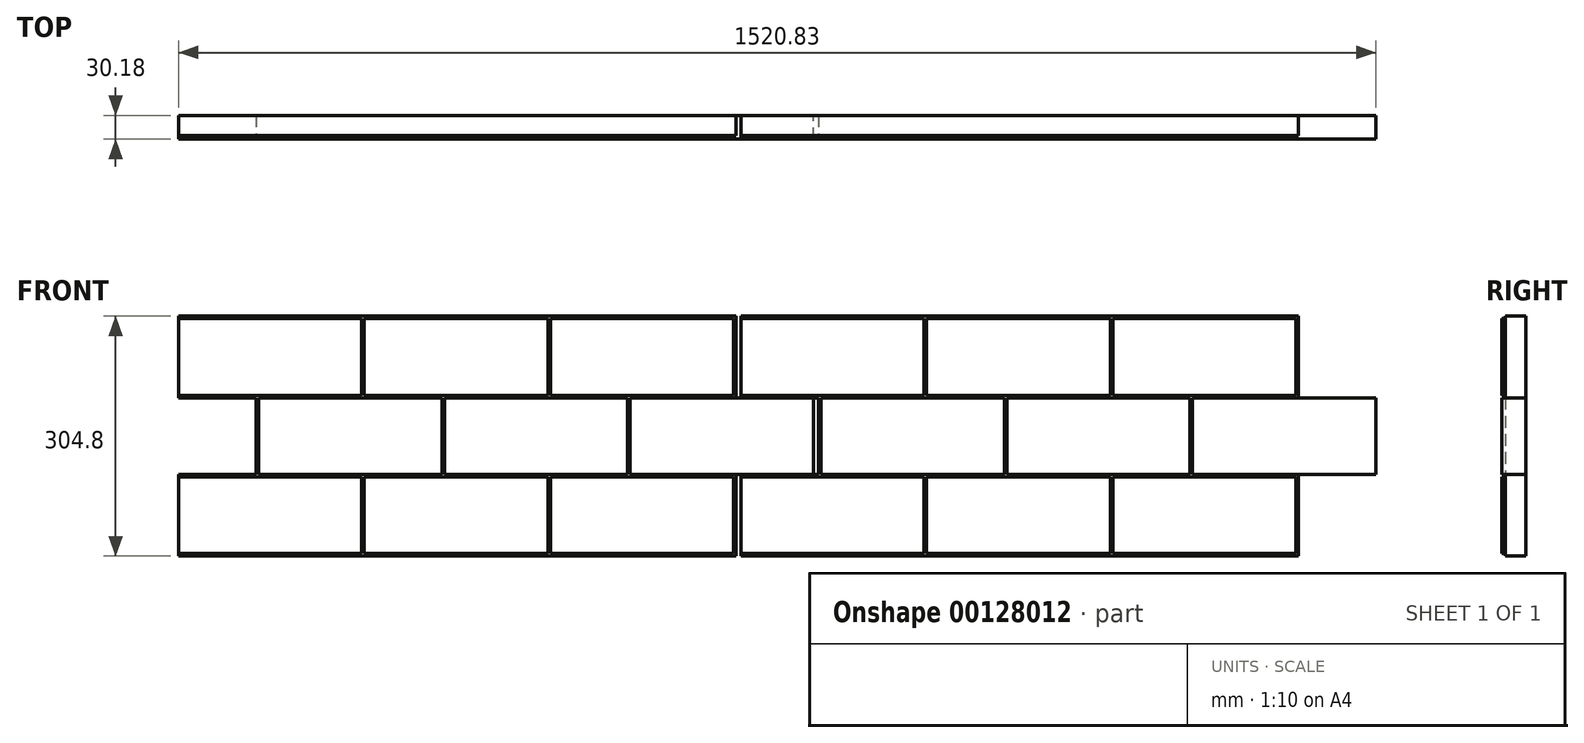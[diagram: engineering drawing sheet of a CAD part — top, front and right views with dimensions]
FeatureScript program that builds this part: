
annotation { "Feature Type Name" : "Feature", "Feature Type Description" : "" }
export const myFeature = defineFeature(function(context is Context, id is Id, definition is map)
    precondition{}
    {
        {
            var Q0;
            Q0=qCreatedBy(makeId("Front.planeOp"),FACE);
            var sketch = newSketch(context, id + "F0", { "sketchPlane" : qUnion([Q0])});
            skLineSegment(sketch, "E0.bottom", {"start": v(-304.8, 152.4) * mm, "end": v(304.8, 152.4) * mm});
            skLineSegment(sketch, "E0.top", {"start": v(-304.8, -152.4) * mm, "end": v(304.8, -152.4) * mm});
            skLineSegment(sketch, "E0.left", {"start": v(-304.8, 152.4) * mm, "end": v(-304.8, -152.4) * mm});
            skPoint(sketch, "E0.middle", {"position": v(0, 0) * mm});
            skLineSegment(sketch, "E1", {"start": v(-304.8, 152.4) * mm, "end": v(-304.8, 149.23) * mm});
            skLineSegment(sketch, "E2", {"start": v(-304.8, 149.23) * mm, "end": v(-304.8, 51.86) * mm});
            skLineSegment(sketch, "E3", {"start": v(-304.8, 51.86) * mm, "end": v(-304.8, 48.68) * mm});
            skLineSegment(sketch, "E4", {"start": v(-304.8, 48.68) * mm, "end": v(-304.8, -48.68) * mm});
            skLineSegment(sketch, "E5", {"start": v(-304.8, -48.68) * mm, "end": v(-304.8, -51.86) * mm});
            skLineSegment(sketch, "E6", {"start": v(-304.8, -51.86) * mm, "end": v(-304.8, -149.22) * mm});
            skLineSegment(sketch, "E7", {"start": v(-304.8, -149.22) * mm, "end": v(-304.8, -152.4) * mm});
            skLineSegment(sketch, "E8", {"start": v(304.8, 152.4) * mm, "end": v(304.8, 149.22) * mm});
            skLineSegment(sketch, "E9", {"start": v(304.8, 149.22) * mm, "end": v(304.8, 51.86) * mm});
            skLineSegment(sketch, "E10", {"start": v(304.8, 48.68) * mm, "end": v(304.8, 51.86) * mm});
            skLineSegment(sketch, "E11", {"start": v(304.8, 48.68) * mm, "end": v(304.8, -48.68) * mm});
            skLineSegment(sketch, "E12", {"start": v(304.8, -48.68) * mm, "end": v(304.8, -51.86) * mm});
            skLineSegment(sketch, "E13", {"start": v(304.8, -149.22) * mm, "end": v(304.8, -152.4) * mm});
            skLineSegment(sketch, "E14", {"start": v(304.8, -51.86) * mm, "end": v(304.8, -149.22) * mm});
            skLineSegment(sketch, "E15.bottom", {"start": v(304.8, 51.86) * mm, "end": v(406.4, 51.86) * mm});
            skLineSegment(sketch, "E15.top", {"start": v(304.8, -51.86) * mm, "end": v(406.4, -51.86) * mm});
            skLineSegment(sketch, "E15.left", {"start": v(304.8, 51.86) * mm, "end": v(304.8, -51.86) * mm});
            skLineSegment(sketch, "E15.right", {"start": v(406.4, 51.86) * mm, "end": v(406.4, -51.86) * mm});
            skLineSegment(sketch, "E16.bottom", {"start": v(-304.8, 152.4) * mm, "end": v(-406.4, 152.4) * mm});
            skLineSegment(sketch, "E16.top", {"start": v(-304.8, 48.68) * mm, "end": v(-406.4, 48.68) * mm});
            skLineSegment(sketch, "E16.left", {"start": v(-304.8, 152.4) * mm, "end": v(-304.8, 48.68) * mm});
            skLineSegment(sketch, "E16.right", {"start": v(-406.4, 152.4) * mm, "end": v(-406.4, 48.68) * mm});
            skLineSegment(sketch, "E17.bottom", {"start": v(-304.8, -48.68) * mm, "end": v(-406.4, -48.68) * mm});
            skLineSegment(sketch, "E17.top", {"start": v(-304.8, -152.4) * mm, "end": v(-406.4, -152.4) * mm});
            skLineSegment(sketch, "E17.left", {"start": v(-304.8, -48.68) * mm, "end": v(-304.8, -152.4) * mm});
            skLineSegment(sketch, "E17.right", {"start": v(-406.4, -48.68) * mm, "end": v(-406.4, -152.4) * mm});
            skSolve(sketch);
        }
        {
            var Q0;
            {var subQ3=sQuery(id+"F0.wireOp",EDGE,"E16.bottom");Q0=makeQuery(id+"F0.imprint","IMPRINT",FACE,{"disambiguationData":[TD([[makeQuery(id+"F0.imprint","IMPRINT",EDGE,{"derivedFrom":subQ3}),1.0]])]});}
            var Q1;
            {var subQ4=sQuery(id+"F0.wireOp",EDGE,"E17.bottom");Q1=makeQuery(id+"F0.imprint","IMPRINT",FACE,{"disambiguationData":[TD([[makeQuery(id+"F0.imprint","IMPRINT",EDGE,{"derivedFrom":subQ4}),1.0]])]});}
            var Q2;
            {var subQ4=sQuery(id+"F0.wireOp",EDGE,"E0.bottom");Q2=makeQuery(id+"F0.imprint","IMPRINT",FACE,{"disambiguationData":[TD([[makeQuery(id+"F0.imprint","IMPRINT",EDGE,{"derivedFrom":subQ4}),-1.0]])]});}
            var Q3;
            {var subQ3=sQuery(id+"F0.wireOp",EDGE,"E15.bottom");Q3=makeQuery(id+"F0.imprint","IMPRINT",FACE,{"disambiguationData":[TD([[makeQuery(id+"F0.imprint","IMPRINT",EDGE,{"derivedFrom":subQ3}),-1.0]])]});}
            extrude(context, id + "F1", {"entities" : qUnion([Q0, Q1, Q2, Q3]), "oppositeDirection" : true, "depth" : 25.4 * mm});
        }
        {
            var Q0;
            Q0=makeQuery(id+"F1.opExtrude","CAP_FACE",FACE,{"disambiguationData":[OSD([sQuery(id+"F0.wireOp",EDGE,"E0.bottom"),sQuery(id+"F0.wireOp",EDGE,"E0.top"),sQuery(id+"F0.wireOp",EDGE,"E4"),sQuery(id+"F0.wireOp",EDGE,"E8"),sQuery(id+"F0.wireOp",EDGE,"E9"),sQuery(id+"F0.wireOp",EDGE,"E13"),sQuery(id+"F0.wireOp",EDGE,"E14"),sQuery(id+"F0.wireOp",EDGE,"E15.bottom"),sQuery(id+"F0.wireOp",EDGE,"E15.top"),sQuery(id+"F0.wireOp",EDGE,"E15.right"),sQuery(id+"F0.wireOp",EDGE,"E16.bottom"),sQuery(id+"F0.wireOp",EDGE,"E16.top"),sQuery(id+"F0.wireOp",EDGE,"E16.right"),sQuery(id+"F0.wireOp",EDGE,"E17.bottom"),sQuery(id+"F0.wireOp",EDGE,"E17.top"),sQuery(id+"F0.wireOp",EDGE,"E17.right")])],"isStart":true});
            var sketch = newSketch(context, id + "F2", { "sketchPlane" : qUnion([Q0])});
            skLineSegment(sketch, "E18.bottom", {"start": v(-406.4, 152.4) * mm, "end": v(-403.23, 152.4) * mm});
            skLineSegment(sketch, "E18.top", {"start": v(-406.4, 149.22) * mm, "end": v(-403.23, 149.22) * mm});
            skLineSegment(sketch, "E18.left", {"start": v(-406.4, 152.4) * mm, "end": v(-406.4, 149.22) * mm});
            skLineSegment(sketch, "E18.right", {"start": v(-403.23, 152.4) * mm, "end": v(-403.22, 149.22) * mm});
            skLineSegment(sketch, "E19.bottom", {"start": v(-406.4, 48.68) * mm, "end": v(-403.23, 48.68) * mm});
            skLineSegment(sketch, "E19.top", {"start": v(-406.4, 51.86) * mm, "end": v(-403.23, 51.86) * mm});
            skLineSegment(sketch, "E19.left", {"start": v(-406.4, 48.68) * mm, "end": v(-406.4, 51.86) * mm});
            skLineSegment(sketch, "E19.right", {"start": v(-403.23, 48.68) * mm, "end": v(-403.23, 51.86) * mm});
            skLineSegment(sketch, "E20.bottom", {"start": v(-403.23, 149.22) * mm, "end": v(-170.56, 149.22) * mm});
            skLineSegment(sketch, "E20.top", {"start": v(-403.23, 51.86) * mm, "end": v(-170.56, 51.86) * mm});
            skLineSegment(sketch, "E20.left", {"start": v(-403.23, 149.22) * mm, "end": v(-403.23, 51.86) * mm});
            skLineSegment(sketch, "E20.right", {"start": v(-170.56, 149.22) * mm, "end": v(-170.56, 51.86) * mm});
            skLineSegment(sketch, "E21.bottom", {"start": v(-406.4, -48.68) * mm, "end": v(-403.23, -48.68) * mm});
            skLineSegment(sketch, "E21.top", {"start": v(-406.4, -51.86) * mm, "end": v(-403.23, -51.86) * mm});
            skLineSegment(sketch, "E21.left", {"start": v(-406.4, -48.68) * mm, "end": v(-406.4, -51.86) * mm});
            skLineSegment(sketch, "E21.right", {"start": v(-403.23, -48.68) * mm, "end": v(-403.23, -51.86) * mm});
            skLineSegment(sketch, "E22.bottom", {"start": v(-406.4, -152.4) * mm, "end": v(-403.23, -152.4) * mm});
            skLineSegment(sketch, "E22.top", {"start": v(-406.4, -149.22) * mm, "end": v(-403.23, -149.22) * mm});
            skLineSegment(sketch, "E22.left", {"start": v(-406.4, -152.4) * mm, "end": v(-406.4, -149.22) * mm});
            skLineSegment(sketch, "E22.right", {"start": v(-403.23, -152.4) * mm, "end": v(-403.23, -149.22) * mm});
            skLineSegment(sketch, "E23.bottom", {"start": v(-403.23, -51.86) * mm, "end": v(-170.56, -51.86) * mm});
            skLineSegment(sketch, "E23.top", {"start": v(-403.23, -149.22) * mm, "end": v(-170.56, -149.22) * mm});
            skLineSegment(sketch, "E23.left", {"start": v(-403.23, -51.86) * mm, "end": v(-403.23, -149.22) * mm});
            skLineSegment(sketch, "E23.right", {"start": v(-170.56, -51.86) * mm, "end": v(-170.56, -149.22) * mm});
            skLineSegment(sketch, "E24.bottom", {"start": v(406.4, 51.86) * mm, "end": v(403.23, 51.86) * mm});
            skLineSegment(sketch, "E24.top", {"start": v(406.4, 48.68) * mm, "end": v(403.23, 48.68) * mm});
            skLineSegment(sketch, "E24.left", {"start": v(406.4, 51.86) * mm, "end": v(406.4, 48.68) * mm});
            skLineSegment(sketch, "E24.right", {"start": v(403.23, 51.86) * mm, "end": v(403.23, 48.68) * mm});
            skLineSegment(sketch, "E25.bottom", {"start": v(406.4, -51.86) * mm, "end": v(403.23, -51.86) * mm});
            skLineSegment(sketch, "E25.top", {"start": v(406.4, -48.68) * mm, "end": v(403.23, -48.68) * mm});
            skLineSegment(sketch, "E25.left", {"start": v(406.4, -51.86) * mm, "end": v(406.4, -48.68) * mm});
            skLineSegment(sketch, "E25.right", {"start": v(403.23, -51.86) * mm, "end": v(403.23, -48.68) * mm});
            skLineSegment(sketch, "E26.bottom", {"start": v(403.23, 48.68) * mm, "end": v(170.3, 48.68) * mm});
            skLineSegment(sketch, "E26.top", {"start": v(403.23, -48.68) * mm, "end": v(170.3, -48.68) * mm});
            skLineSegment(sketch, "E26.left", {"start": v(403.23, 48.68) * mm, "end": v(403.23, -48.68) * mm});
            skLineSegment(sketch, "E26.right", {"start": v(170.3, 48.68) * mm, "end": v(170.3, -48.68) * mm});
            skLineSegment(sketch, "E27.bottom", {"start": v(304.8, -152.4) * mm, "end": v(301.62, -152.4) * mm});
            skLineSegment(sketch, "E27.top", {"start": v(304.8, -149.22) * mm, "end": v(301.62, -149.22) * mm});
            skLineSegment(sketch, "E27.left", {"start": v(304.8, -152.4) * mm, "end": v(304.8, -149.22) * mm});
            skLineSegment(sketch, "E27.right", {"start": v(301.62, -152.4) * mm, "end": v(301.62, -149.22) * mm});
            skLineSegment(sketch, "E28.bottom", {"start": v(304.8, 152.4) * mm, "end": v(301.62, 152.4) * mm});
            skLineSegment(sketch, "E28.top", {"start": v(304.8, 149.22) * mm, "end": v(301.62, 149.22) * mm});
            skLineSegment(sketch, "E28.left", {"start": v(304.8, 152.4) * mm, "end": v(304.8, 149.22) * mm});
            skLineSegment(sketch, "E28.right", {"start": v(301.62, 152.4) * mm, "end": v(301.62, 149.22) * mm});
            skLineSegment(sketch, "E29.bottom", {"start": v(301.62, 149.22) * mm, "end": v(68.96, 149.22) * mm});
            skLineSegment(sketch, "E29.top", {"start": v(301.62, 51.86) * mm, "end": v(68.96, 51.86) * mm});
            skLineSegment(sketch, "E29.left", {"start": v(301.62, 149.22) * mm, "end": v(301.62, 51.86) * mm});
            skLineSegment(sketch, "E29.right", {"start": v(68.96, 149.22) * mm, "end": v(68.96, 51.86) * mm});
            skLineSegment(sketch, "E30.bottom", {"start": v(301.62, -149.22) * mm, "end": v(68.96, -149.22) * mm});
            skLineSegment(sketch, "E30.top", {"start": v(301.62, -51.86) * mm, "end": v(68.96, -51.86) * mm});
            skLineSegment(sketch, "E30.left", {"start": v(301.62, -149.22) * mm, "end": v(301.62, -51.86) * mm});
            skLineSegment(sketch, "E30.right", {"start": v(68.96, -149.22) * mm, "end": v(68.96, -51.86) * mm});
            skLineSegment(sketch, "E31", {"start": v(-170.56, 149.22) * mm, "end": v(-167.39, 149.22) * mm});
            skLineSegment(sketch, "E32.bottom", {"start": v(-167.39, 149.22) * mm, "end": v(65.79, 149.22) * mm});
            skLineSegment(sketch, "E32.top", {"start": v(-167.39, 51.86) * mm, "end": v(65.79, 51.86) * mm});
            skLineSegment(sketch, "E32.left", {"start": v(-167.39, 149.22) * mm, "end": v(-167.39, 51.86) * mm});
            skLineSegment(sketch, "E32.right", {"start": v(65.79, 149.22) * mm, "end": v(65.79, 51.86) * mm});
            skLineSegment(sketch, "E33", {"start": v(65.79, 149.22) * mm, "end": v(68.96, 149.22) * mm});
            skLineSegment(sketch, "E34", {"start": v(-170.56, -51.86) * mm, "end": v(-167.39, -51.86) * mm});
            skLineSegment(sketch, "E35", {"start": v(68.96, -51.86) * mm, "end": v(65.79, -51.86) * mm});
            skLineSegment(sketch, "E36.bottom", {"start": v(-167.39, -51.86) * mm, "end": v(65.79, -51.86) * mm});
            skLineSegment(sketch, "E36.top", {"start": v(-167.39, -149.22) * mm, "end": v(65.79, -149.22) * mm});
            skLineSegment(sketch, "E36.left", {"start": v(-167.39, -51.86) * mm, "end": v(-167.39, -149.22) * mm});
            skLineSegment(sketch, "E36.right", {"start": v(65.79, -51.86) * mm, "end": v(65.79, -149.22) * mm});
            skLineSegment(sketch, "E37", {"start": v(170.3, 48.68) * mm, "end": v(167.13, 48.68) * mm});
            skLineSegment(sketch, "E38.bottom", {"start": v(167.13, 48.68) * mm, "end": v(-65.53, 48.68) * mm});
            skLineSegment(sketch, "E38.top", {"start": v(167.13, -48.68) * mm, "end": v(-65.53, -48.68) * mm});
            skLineSegment(sketch, "E38.left", {"start": v(167.13, 48.68) * mm, "end": v(167.13, -48.68) * mm});
            skLineSegment(sketch, "E38.right", {"start": v(-65.53, 48.68) * mm, "end": v(-65.53, -48.68) * mm});
            skLineSegment(sketch, "E39", {"start": v(-65.53, 48.68) * mm, "end": v(-68.7, 48.68) * mm});
            skLineSegment(sketch, "E40.bottom", {"start": v(-68.7, 48.68) * mm, "end": v(-301.62, 48.68) * mm});
            skLineSegment(sketch, "E40.top", {"start": v(-68.7, -48.68) * mm, "end": v(-301.62, -48.68) * mm});
            skLineSegment(sketch, "E40.left", {"start": v(-68.7, 48.68) * mm, "end": v(-68.7, -48.68) * mm});
            skLineSegment(sketch, "E40.right", {"start": v(-301.62, 48.68) * mm, "end": v(-301.62, -48.68) * mm});
            skSolve(sketch);
        }
        {
            var Q0;
            Q0=makeQuery(id+"F2.imprint","IMPRINT",FACE,{"disambiguationData":[TD([[makeQuery(id+"F2.imprint","IMPRINT",EDGE,{"derivedFrom":sQuery(id+"F2.wireOp",EDGE,"E32.bottom")}),-1.0]])]});
            var Q1;
            Q1=makeQuery(id+"F2.imprint","IMPRINT",FACE,{"disambiguationData":[TD([[makeQuery(id+"F2.imprint","IMPRINT",EDGE,{"derivedFrom":sQuery(id+"F2.wireOp",EDGE,"E20.bottom")}),-1.0]])]});
            var Q2;
            Q2=makeQuery(id+"F2.imprint","IMPRINT",FACE,{"disambiguationData":[TD([[makeQuery(id+"F2.imprint","IMPRINT",EDGE,{"derivedFrom":sQuery(id+"F2.wireOp",EDGE,"E26.bottom")}),1.0]])]});
            var Q3;
            Q3=makeQuery(id+"F2.imprint","IMPRINT",FACE,{"disambiguationData":[TD([[makeQuery(id+"F2.imprint","IMPRINT",EDGE,{"derivedFrom":sQuery(id+"F2.wireOp",EDGE,"E38.bottom")}),1.0]])]});
            extrude(context, id + "F3", {"entities" : qUnion([Q0, Q1, Q2, Q3]), "operationType" : NewBodyOperationType.ADD, "depth" : 4.78 * mm});
        }
        {
            var Q0;
            Q0=makeQuery(id+"F2.imprint","IMPRINT",FACE,{"disambiguationData":[TD([[makeQuery(id+"F2.imprint","IMPRINT",EDGE,{"derivedFrom":sQuery(id+"F2.wireOp",EDGE,"E23.bottom")}),-1.0]])]});
            var Q1;
            Q1=makeQuery(id+"F2.imprint","IMPRINT",FACE,{"disambiguationData":[TD([[makeQuery(id+"F2.imprint","IMPRINT",EDGE,{"derivedFrom":sQuery(id+"F2.wireOp",EDGE,"E40.bottom")}),1.0]])]});
            var Q2;
            Q2=makeQuery(id+"F2.imprint","IMPRINT",FACE,{"disambiguationData":[TD([[makeQuery(id+"F2.imprint","IMPRINT",EDGE,{"derivedFrom":sQuery(id+"F2.wireOp",EDGE,"E36.bottom")}),-1.0]])]});
            var Q3;
            Q3=makeQuery(id+"F2.imprint","IMPRINT",FACE,{"disambiguationData":[TD([[makeQuery(id+"F2.imprint","IMPRINT",EDGE,{"derivedFrom":sQuery(id+"F2.wireOp",EDGE,"E30.bottom")}),-1.0]])]});
            var Q4;
            Q4=makeQuery(id+"F2.imprint","IMPRINT",FACE,{"disambiguationData":[TD([[makeQuery(id+"F2.imprint","IMPRINT",EDGE,{"derivedFrom":sQuery(id+"F2.wireOp",EDGE,"E29.bottom")}),1.0]])]});
            extrude(context, id + "F4", {"entities" : qUnion([Q0, Q1, Q2, Q3, Q4]), "operationType" : NewBodyOperationType.ADD, "depth" : 4.78 * mm});
        }
        {
            var Q0;
            {var subQ7=sQuery(id+"F2.wireOp",EDGE,"E19.right");Q0=makeQuery(id+"F2.imprint","IMPRINT",FACE,{"disambiguationData":[TD([[makeQuery(id+"F2.imprint","IMPRINT",EDGE,{"derivedFrom":subQ7}),-1.0]])]});}
            var sketch = newSketch(context, id + "F5", { "sketchPlane" : qUnion([Q0])});
            skLineSegment(sketch, "E41.bottom", {"start": v(304.8, 51.86) * mm, "end": v(406.4, 51.86) * mm});
            skLineSegment(sketch, "E41.top", {"start": v(304.8, 48.68) * mm, "end": v(406.4, 48.68) * mm});
            skLineSegment(sketch, "E41.left", {"start": v(304.8, 51.86) * mm, "end": v(304.8, 48.68) * mm});
            skLineSegment(sketch, "E41.right", {"start": v(406.4, 51.86) * mm, "end": v(406.4, 48.68) * mm});
            skLineSegment(sketch, "E42.bottom", {"start": v(406.4, 48.68) * mm, "end": v(403.23, 48.68) * mm});
            skLineSegment(sketch, "E42.top", {"start": v(406.4, -51.86) * mm, "end": v(403.23, -51.86) * mm});
            skLineSegment(sketch, "E42.left", {"start": v(406.4, 48.68) * mm, "end": v(406.4, -51.86) * mm});
            skLineSegment(sketch, "E42.right", {"start": v(403.23, 48.68) * mm, "end": v(403.23, -51.86) * mm});
            skLineSegment(sketch, "E43.bottom", {"start": v(403.23, -51.86) * mm, "end": v(304.8, -51.86) * mm});
            skLineSegment(sketch, "E43.top", {"start": v(403.23, -48.68) * mm, "end": v(304.8, -48.68) * mm});
            skLineSegment(sketch, "E43.left", {"start": v(403.23, -51.86) * mm, "end": v(403.23, -48.68) * mm});
            skLineSegment(sketch, "E43.right", {"start": v(304.8, -51.86) * mm, "end": v(304.8, -48.68) * mm});
            skSolve(sketch);
        }
        {
            var Q0;
            Q0 = qSketchRegion(id + "F5", true);
            extrude(context, id + "F6", {"entities" : qUnion([Q0]), "operationType" : NewBodyOperationType.REMOVE, "oppositeDirection" : true, "depth" : 25.4 * mm});
        }
        {
            var Q0;
            {var subQ0=sQuery(id+"F2.wireOp",EDGE,"E18.top");Q0=makeQuery(id+"F2.imprint","IMPRINT",FACE,{"disambiguationData":[TD([[makeQuery(id+"F2.imprint","IMPRINT",EDGE,{"derivedFrom":subQ0}),-1.0]])]});}
            var sketch = newSketch(context, id + "F7", { "sketchPlane" : qUnion([Q0])});
            skLineSegment(sketch, "E44.bottom", {"start": v(-406.4, 152.4) * mm, "end": v(-403.23, 152.4) * mm});
            skLineSegment(sketch, "E44.top", {"start": v(-406.4, -152.4) * mm, "end": v(-403.23, -152.4) * mm});
            skLineSegment(sketch, "E44.left", {"start": v(-406.4, 152.4) * mm, "end": v(-406.4, -152.4) * mm});
            skLineSegment(sketch, "E44.right", {"start": v(-403.23, 152.4) * mm, "end": v(-403.23, -152.4) * mm});
            skSolve(sketch);
        }
        {
            var Q0;
            Q0 = qSketchRegion(id + "F7", true);
            extrude(context, id + "F8", {"entities" : qUnion([Q0]), "operationType" : NewBodyOperationType.REMOVE, "oppositeDirection" : true, "depth" : 25.4 * mm});
        }
        {
            var Q0;
            Q0=makeQuery(id+"F1.opExtrude","SWEPT_BODY",BODY,{"disambiguationData":[OSD([sQuery(id+"F0.wireOp",EDGE,"E0.bottom"),sQuery(id+"F0.wireOp",EDGE,"E0.top"),sQuery(id+"F0.wireOp",EDGE,"E4"),sQuery(id+"F0.wireOp",EDGE,"E8"),sQuery(id+"F0.wireOp",EDGE,"E9"),sQuery(id+"F0.wireOp",EDGE,"E13"),sQuery(id+"F0.wireOp",EDGE,"E14"),sQuery(id+"F0.wireOp",EDGE,"E15.bottom"),sQuery(id+"F0.wireOp",EDGE,"E15.top"),sQuery(id+"F0.wireOp",EDGE,"E15.right"),sQuery(id+"F0.wireOp",EDGE,"E16.bottom"),sQuery(id+"F0.wireOp",EDGE,"E16.top"),sQuery(id+"F0.wireOp",EDGE,"E16.right"),sQuery(id+"F0.wireOp",EDGE,"E17.bottom"),sQuery(id+"F0.wireOp",EDGE,"E17.top"),sQuery(id+"F0.wireOp",EDGE,"E17.right")])]});
            transform(context, id + "F9", {"entities" : qUnion([Q0]), "transformType" : TransformType.TRANSLATION_3D, "dx" : 708.02 * mm, "dy" : 0 * mm, "dz" : 0 * mm, "makeCopy" : true});
        }
        {
            var Q0;
            Q0=makeQuery(id+"F9.opPattern","COPY",BODY,{"derivedFrom":makeQuery(id+"F1.opExtrude","SWEPT_BODY",BODY,{"disambiguationData":[OSD([sQuery(id+"F0.wireOp",EDGE,"E0.bottom"),sQuery(id+"F0.wireOp",EDGE,"E0.top"),sQuery(id+"F0.wireOp",EDGE,"E4"),sQuery(id+"F0.wireOp",EDGE,"E8"),sQuery(id+"F0.wireOp",EDGE,"E9"),sQuery(id+"F0.wireOp",EDGE,"E13"),sQuery(id+"F0.wireOp",EDGE,"E14"),sQuery(id+"F0.wireOp",EDGE,"E15.bottom"),sQuery(id+"F0.wireOp",EDGE,"E15.top"),sQuery(id+"F0.wireOp",EDGE,"E15.right"),sQuery(id+"F0.wireOp",EDGE,"E16.bottom"),sQuery(id+"F0.wireOp",EDGE,"E16.top"),sQuery(id+"F0.wireOp",EDGE,"E16.right"),sQuery(id+"F0.wireOp",EDGE,"E17.bottom"),sQuery(id+"F0.wireOp",EDGE,"E17.top"),sQuery(id+"F0.wireOp",EDGE,"E17.right")])]}),"instanceName":"1"});
            transform(context, id + "F10", {"entities" : qUnion([Q0]), "transformType" : TransformType.TRANSLATION_3D, "dx" : 6.35 * mm, "dy" : 0 * mm, "dz" : 0 * mm, "makeCopy" : false});
        }
    });
